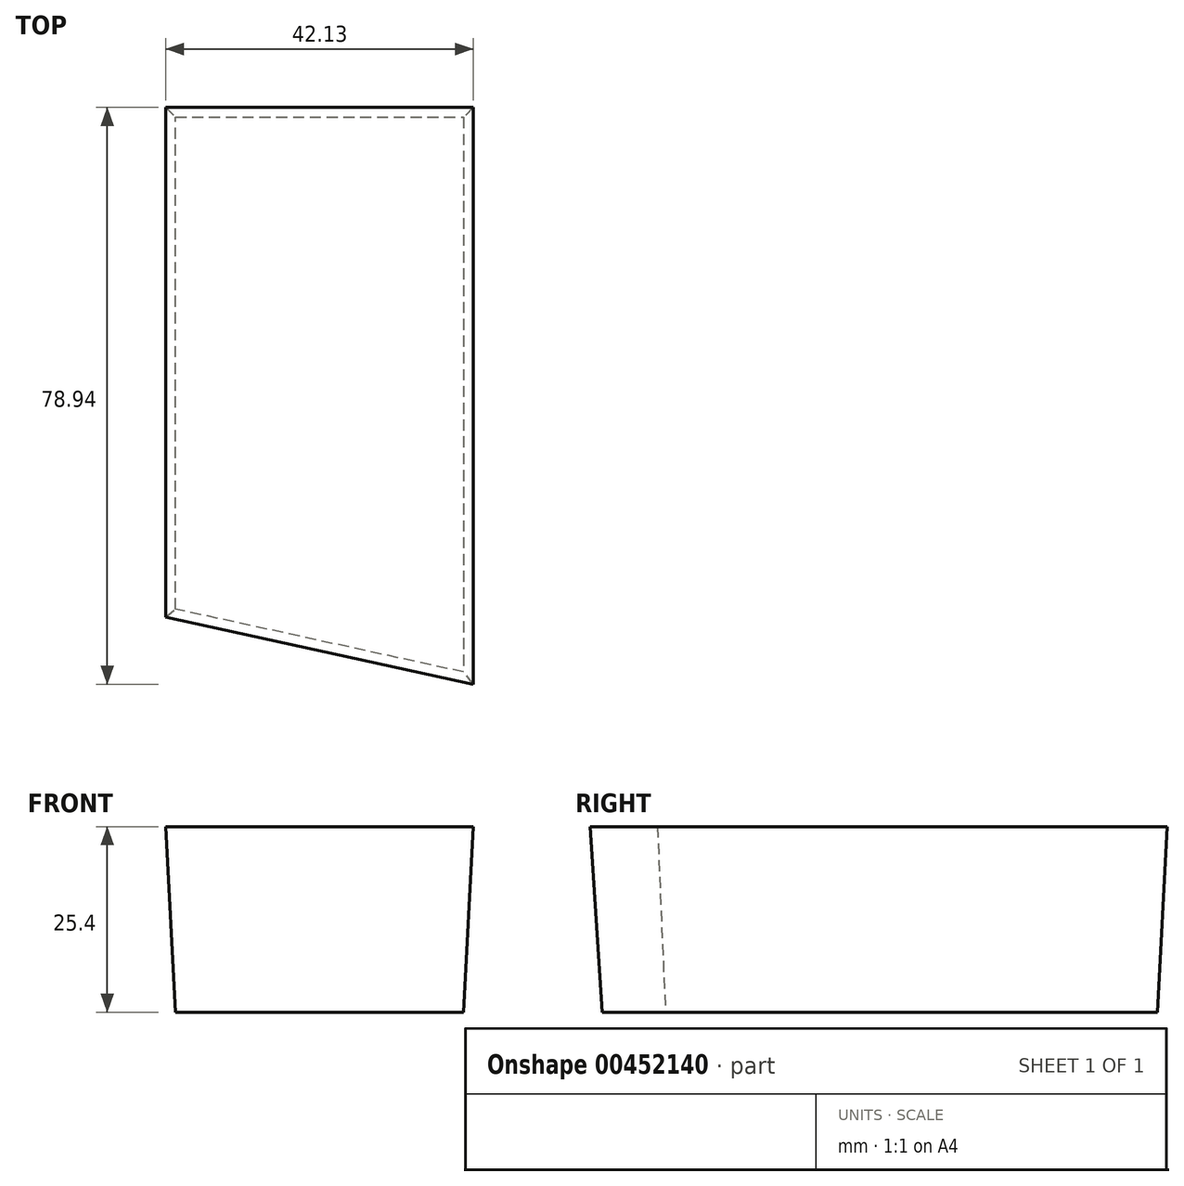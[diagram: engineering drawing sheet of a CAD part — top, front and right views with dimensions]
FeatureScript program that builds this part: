
annotation { "Feature Type Name" : "Feature", "Feature Type Description" : "" }
export const myFeature = defineFeature(function(context is Context, id is Id, definition is map)
    precondition{}
    {
        {
            var Q0;
            Q0=qCreatedBy(makeId("Top.planeOp"),FACE);
            var sketch = newSketch(context, id + "F0", { "sketchPlane" : qUnion([Q0])});
            skLineSegment(sketch, "E0", {"start": v(-133.58, -52.32) * mm, "end": v(-133.58, 15.02) * mm});
            skLineSegment(sketch, "E1", {"start": v(-133.58, 15.02) * mm, "end": v(-94.11, 15.02) * mm});
            skLineSegment(sketch, "E2", {"start": v(-94.11, 15.02) * mm, "end": v(-94.11, -60.94) * mm});
            skLineSegment(sketch, "E3", {"start": v(-94.11, -60.94) * mm, "end": v(-133.58, -52.32) * mm});
            skSolve(sketch);
        }
        {
            var Q0;
            Q0=makeQuery(id+"F0.imprint","IMPRINT",FACE,{"disambiguationData":[TD([[makeQuery(id+"F0.imprint","IMPRINT",EDGE,{"derivedFrom":sQuery(id+"F0.wireOp",EDGE,"E0")}),-1.0]])]});
            extrude(context, id + "F1", {"entities" : qUnion([Q0]), "depth" : 25.4 * mm, "hasDraft" : true, "draftAngle" : 3 * degree});
        }
    });
